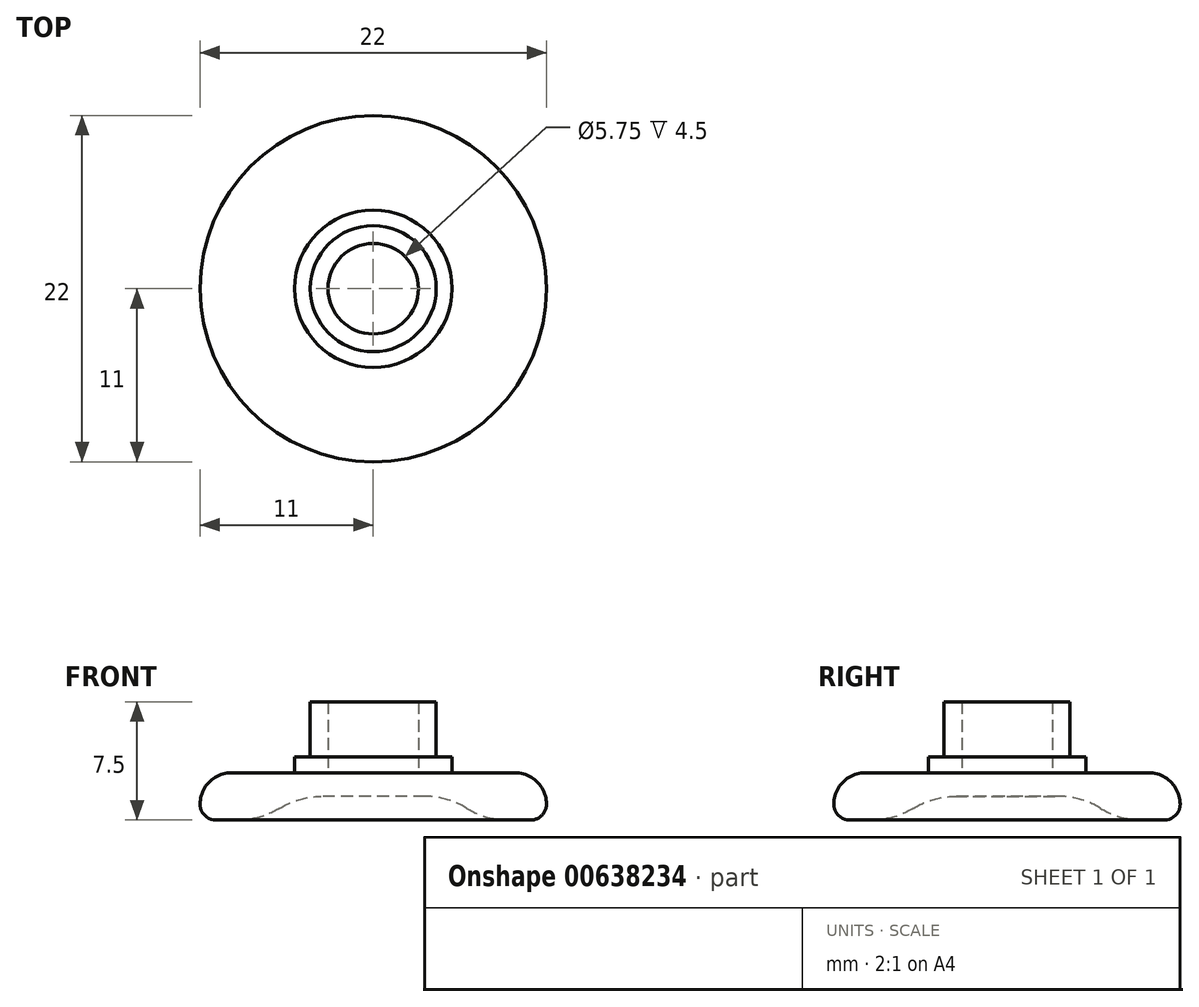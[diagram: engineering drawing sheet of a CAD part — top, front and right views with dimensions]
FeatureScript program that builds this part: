
annotation { "Feature Type Name" : "Feature", "Feature Type Description" : "" }
export const myFeature = defineFeature(function(context is Context, id is Id, definition is map)
    precondition{}
    {
        {
            assignVariable(context, id + "F0", {"name" : "PlateThickness", "anyValue" : 3});
        }
        {
            var Q0;
            Q0=qCreatedBy(makeId("Top.planeOp"),FACE);
            var sketch = newSketch(context, id + "F1", { "sketchPlane" : qUnion([Q0])});
            skCircle(sketch, "E0", {"center": v(0, 0) * mm, "radius": 11 * mm});
            skCircle(sketch, "E1", {"center": v(0, 0) * mm, "radius": 4 * mm});
            skCircle(sketch, "E2", {"center": v(0, 0) * mm, "radius": 2.88 * mm});
            skCircle(sketch, "E3", {"center": v(0, 0) * mm, "radius": 5 * mm});
            skSolve(sketch);
        }
        {
            var Q0;
            Q0=makeQuery(id+"F1.imprint","IMPRINT",FACE,{"disambiguationData":[TD([[makeQuery(id+"F1.imprint","IMPRINT",EDGE,{"derivedFrom":sQuery(id+"F1.wireOp",EDGE,"E0")}),1.0]])]});
            var Q1;
            Q1=makeQuery(id+"F1.imprint","IMPRINT",FACE,{"disambiguationData":[TD([[makeQuery(id+"F1.imprint","IMPRINT",EDGE,{"derivedFrom":sQuery(id+"F1.wireOp",EDGE,"E1")}),-1.0]])]});
            extrude(context, id + "F2", {"entities" : qUnion([Q0, Q1]), "depth" : (getVariable(context, 'PlateThickness')) * mm, "offsetDistance" : 25 * mm});
        }
        {
            var Q0;
            Q0=makeQuery(id+"F1.imprint","IMPRINT",FACE,{"disambiguationData":[TD([[makeQuery(id+"F1.imprint","IMPRINT",EDGE,{"derivedFrom":sQuery(id+"F1.wireOp",EDGE,"E1")}),1.0]])]});
            extrude(context, id + "F3", {"entities" : qUnion([Q0]), "operationType" : NewBodyOperationType.ADD, "depth" : (getVariable(context, 'PlateThickness') + 4.5) * mm, "offsetDistance" : 25 * mm});
        }
        {
            var Q0;
            Q0=makeQuery(id+"F1.imprint","IMPRINT",FACE,{"disambiguationData":[TD([[makeQuery(id+"F1.imprint","IMPRINT",EDGE,{"derivedFrom":sQuery(id+"F1.wireOp",EDGE,"E2")}),1.0]])]});
            extrude(context, id + "F4", {"entities" : qUnion([Q0]), "operationType" : NewBodyOperationType.ADD, "depth" : (getVariable(context, 'PlateThickness')) * mm, "offsetDistance" : 25 * mm, "hasSecondDirection" : true, "secondDirectionOppositeDirection" : false, "secondDirectionDepth" : 1.5 * mm});
        }
        {
            var Q0;
            Q0=makeQuery(id+"F1.imprint","IMPRINT",FACE,{"disambiguationData":[TD([[makeQuery(id+"F1.imprint","IMPRINT",EDGE,{"derivedFrom":sQuery(id+"F1.wireOp",EDGE,"E1")}),-1.0]])]});
            var Q1;
            Q1=makeQuery(id+"F2.opExtrude","CAP_FACE",FACE,{"disambiguationData":[OSD([sQuery(id+"F1.wireOp",EDGE,"E0"),sQuery(id+"F1.wireOp",EDGE,"E1")])],"isStart":false});
            extrude(context, id + "F5", {"entities" : qUnion([Q0]), "operationType" : NewBodyOperationType.ADD, "depth" : (getVariable(context, 'PlateThickness') + 1) * mm, "offsetDistance" : 25 * mm, "hasSecondDirection" : true, "secondDirectionBound" : SecondDirectionBoundingType.UP_TO_SURFACE, "secondDirectionOppositeDirection" : false, "secondDirectionDepth" : 25 * mm, "secondDirectionBoundEntityFace" : qUnion([Q1])});
        }
        {
            var Q0;
            Q0=makeQuery(id+"F2.opExtrude","CAP_EDGE",EDGE,{"disambiguationData":[OSD([sQuery(id+"F1.wireOp",EDGE,"E0")])],"isStart":true});
            fillet(context, id + "F6", {"entities" : qUnion([Q0]), "radius" : 1 * mm, "tangentPropagation" : true, "allowEdgeOverflow" : false});
        }
        {
            var Q0;
            Q0=makeQuery(id+"F3.opExtrude","CAP_EDGE",EDGE,{"disambiguationData":[OSD([sQuery(id+"F1.wireOp",EDGE,"E2")])],"isStart":true});
            chamfer(context, id + "F7", {"entities" : qUnion([Q0]), "width" : 4 * mm, "tangentPropagation" : true});
        }
        {
            var Q0;
            {var subQ0=sQuery(id+"F1.wireOp",EDGE,"E2");Q0=makeQuery(id+"F7.opChamfer","BLEND_EDGE",EDGE,{"blendedFrom":[makeQuery(id+"F3.opExtrude","CAP_EDGE",EDGE,{"disambiguationData":[OSD([subQ0])],"isStart":true}),makeQuery(id+"F4.opExtrude","CAP_FACE",FACE,{"disambiguationData":[OSD([subQ0])],"isStart":true})],"blendedInto":[makeQuery(id+"F4.opExtrude","CAP_FACE",FACE,{"disambiguationData":[OSD([subQ0])],"isStart":true})]});}
            fillet(context, id + "F8", {"entities" : qUnion([Q0]), "radius" : 5 * mm, "tangentPropagation" : true, "allowEdgeOverflow" : false});
        }
        {
            var Q0;
            {var subQ0=sQuery(id+"F1.wireOp",EDGE,"E2");var subQ1=sQuery(id+"F1.wireOp",EDGE,"E1");Q0=makeQuery(id+"F7.opChamfer","BLEND_EDGE",EDGE,{"blendedFrom":[makeQuery(id+"F3.opExtrude","CAP_EDGE",EDGE,{"disambiguationData":[OSD([subQ0])],"isStart":true}),makeQuery(id+"F3.boolean.opBoolean","MERGE",FACE,{"derivedFrom":[makeQuery(id+"F2.opExtrude","CAP_FACE",FACE,{"disambiguationData":[OSD([sQuery(id+"F1.wireOp",EDGE,"E0"),subQ1])],"isStart":true}),makeQuery(id+"F3.opExtrude","CAP_FACE",FACE,{"disambiguationData":[OSD([subQ1,subQ0])],"isStart":true})]})],"blendedInto":[makeQuery(id+"F3.boolean.opBoolean","MERGE",FACE,{"derivedFrom":[makeQuery(id+"F2.opExtrude","CAP_FACE",FACE,{"disambiguationData":[OSD([sQuery(id+"F1.wireOp",EDGE,"E0"),subQ1])],"isStart":true}),makeQuery(id+"F3.opExtrude","CAP_FACE",FACE,{"disambiguationData":[OSD([subQ1,subQ0])],"isStart":true})]})]});}
            fillet(context, id + "F9", {"entities" : qUnion([Q0]), "radius" : 5 * mm, "tangentPropagation" : true, "allowEdgeOverflow" : false});
        }
        {
            var Q0;
            Q0=makeQuery(id+"F2.opExtrude","CAP_EDGE",EDGE,{"disambiguationData":[OSD([sQuery(id+"F1.wireOp",EDGE,"E0")])],"isStart":false});
            fillet(context, id + "F10", {"entities" : qUnion([Q0]), "radius" : 2 * mm, "tangentPropagation" : true, "allowEdgeOverflow" : false});
        }
    });
